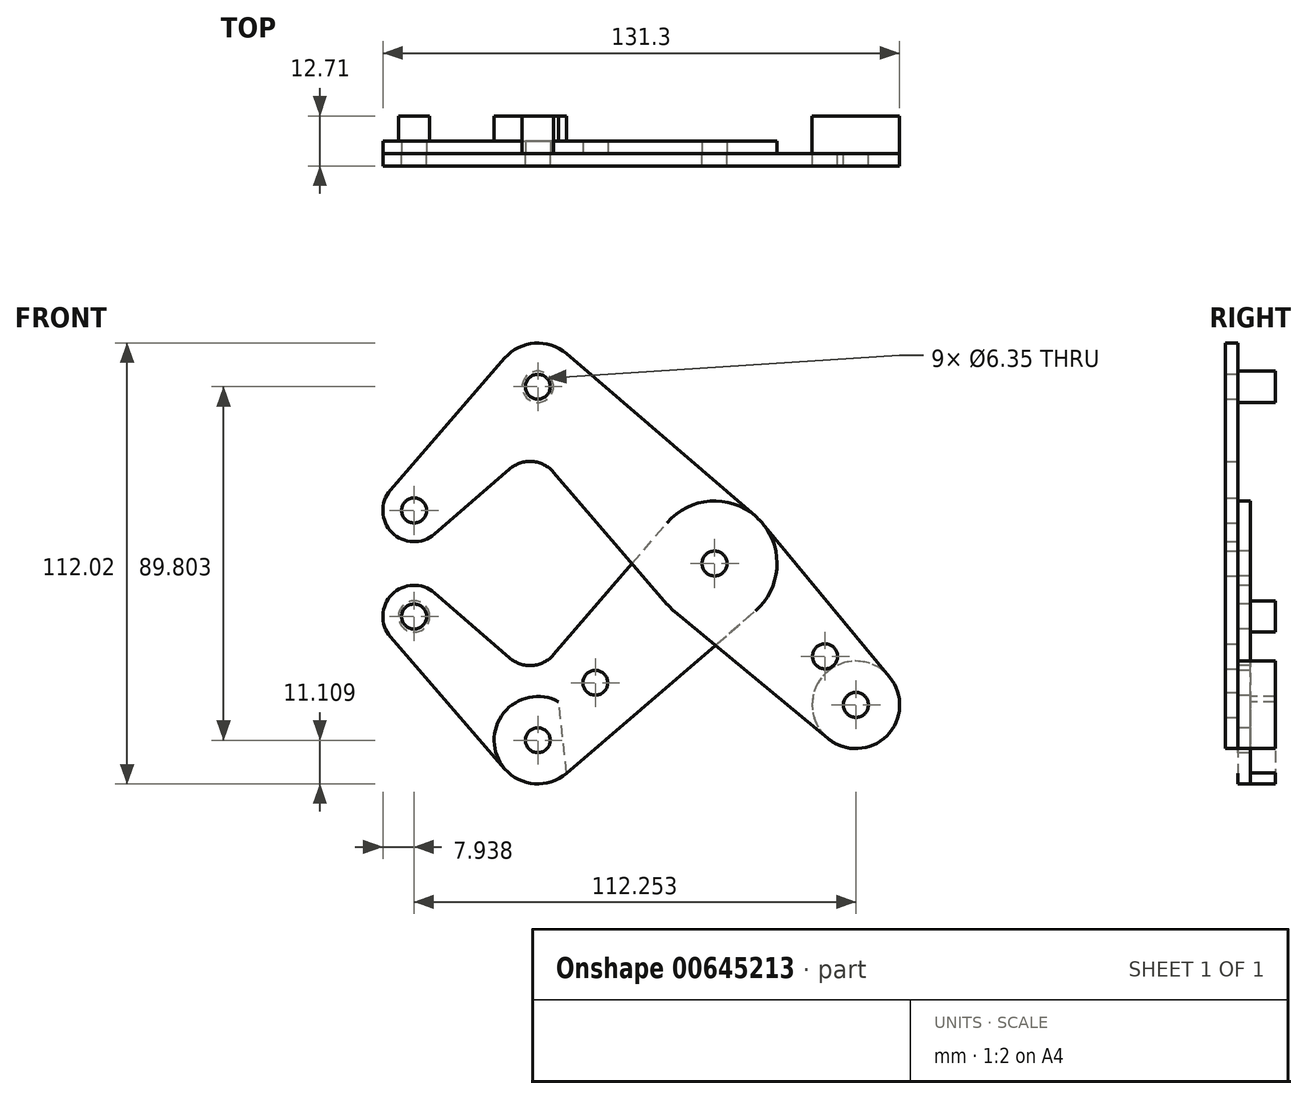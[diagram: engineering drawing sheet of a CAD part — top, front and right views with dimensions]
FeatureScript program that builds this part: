
annotation { "Feature Type Name" : "Feature", "Feature Type Description" : "" }
export const myFeature = defineFeature(function(context is Context, id is Id, definition is map)
    precondition{}
    {
        {
            var Q0;
            Q0=qCreatedBy(makeId("Front.planeOp"),FACE);
            var sketch = newSketch(context, id + "F0", { "sketchPlane" : qUnion([Q0])});
            skLineSegment(sketch, "E0", {"start": v(-76.33, 13.47) * mm, "end": v(-44.9, 44.9) * mm, "construction": true});
            skLineSegment(sketch, "E1", {"start": v(-44.9, 44.9) * mm, "end": v(35.92, -35.92) * mm, "construction": true});
            skCircle(sketch, "E2", {"center": v(-76.33, 13.47) * mm, "radius": 3.18 * mm});
            skCircle(sketch, "E3", {"center": v(-76.33, 13.47) * mm, "radius": 7.94 * mm});
            skCircle(sketch, "E4", {"center": v(-44.9, 44.9) * mm, "radius": 3.18 * mm});
            skCircle(sketch, "E5", {"center": v(-44.9, 44.9) * mm, "radius": 11.11 * mm});
            skCircle(sketch, "E6", {"center": v(0, 0) * mm, "radius": 15.88 * mm});
            skCircle(sketch, "E7", {"center": v(0, 0) * mm, "radius": 3.98 * mm});
            skCircle(sketch, "E8", {"center": v(0, 0) * mm, "radius": 3.18 * mm});
            skCircle(sketch, "E9", {"center": v(35.92, -35.92) * mm, "radius": 11.11 * mm});
            skCircle(sketch, "E10", {"center": v(35.92, -35.92) * mm, "radius": 3.18 * mm});
            skCircle(sketch, "E11", {"center": v(28.07, -23.58) * mm, "radius": 3.18 * mm});
            skLineSegment(sketch, "E12", {"start": v(0, 0) * mm, "end": v(28.01, 28.01) * mm, "construction": true});
            skLineSegment(sketch, "E13", {"start": v(-53.3, 52.18) * mm, "end": v(-82.33, 18.67) * mm});
            skLineSegment(sketch, "E14", {"start": v(-71.13, 7.47) * mm, "end": v(-52.08, 23.98) * mm});
            skLineSegment(sketch, "E15", {"start": v(-40.85, 23.15) * mm, "end": v(-12.04, -10.35) * mm});
            skLineSegment(sketch, "E16", {"start": v(-37.66, 53.33) * mm, "end": v(11.26, 11.26) * mm});
            skLineSegment(sketch, "E17", {"start": v(-10.12, -12.23) * mm, "end": v(28.83, -44.48) * mm});
            skLineSegment(sketch, "E18", {"start": v(12.23, 10.12) * mm, "end": v(44.48, -28.83) * mm});
            skArc(sketch, "E19.filletArc", {"start": v(-40.85, 23.15) * mm, "mid": v(-46.3, 25.9) * mm, "end": v(-52.08, 23.98) * mm});
            skLineSegment(sketch, "E20", {"start": v(0, 0) * mm, "end": v(-44.9, -44.9) * mm, "construction": true});
            skLineSegment(sketch, "E21", {"start": v(-44.9, -44.9) * mm, "end": v(-76.33, -13.47) * mm, "construction": true});
            skCircle(sketch, "E22", {"center": v(-30.3, -30.3) * mm, "radius": 3.18 * mm});
            skCircle(sketch, "E23", {"center": v(-44.9, -44.9) * mm, "radius": 11.11 * mm});
            skCircle(sketch, "E24", {"center": v(-44.9, -44.9) * mm, "radius": 3.18 * mm});
            skCircle(sketch, "E25", {"center": v(-76.33, -13.47) * mm, "radius": 7.94 * mm});
            skCircle(sketch, "E26", {"center": v(-76.33, -13.47) * mm, "radius": 3.18 * mm});
            skLineSegment(sketch, "E27", {"start": v(-82.33, -18.67) * mm, "end": v(-53.3, -52.18) * mm});
            skLineSegment(sketch, "E28", {"start": v(-71.13, -7.47) * mm, "end": v(-52.08, -23.98) * mm});
            skLineSegment(sketch, "E29", {"start": v(-40.85, -23.15) * mm, "end": v(-12.04, 10.35) * mm});
            skLineSegment(sketch, "E30", {"start": v(-37.66, -53.33) * mm, "end": v(10.35, -12.04) * mm});
            skArc(sketch, "E31.filletArc", {"start": v(-52.08, -23.98) * mm, "mid": v(-46.3, -25.9) * mm, "end": v(-40.85, -23.15) * mm});
            skSolve(sketch);
        }
        {
            var Q0;
            Q0=makeQuery(id+"F0.imprint","IMPRINT",FACE,{"disambiguationData":[TD([[makeQuery(id+"F0.imprint","IMPRINT",EDGE,{"derivedFrom":sQuery(id+"F0.wireOp",EDGE,"E2")}),-1.0]])]});
            var Q1;
            {var subQ0=sQuery(id+"F0.wireOp",EDGE,"E13");Q1=makeQuery(id+"F0.imprint","IMPRINT",FACE,{"disambiguationData":[TD([[makeQuery(id+"F0.imprint","IMPRINT",EDGE,{"derivedFrom":subQ0}),1.0]])]});}
            var Q2;
            Q2=makeQuery(id+"F0.imprint","IMPRINT",FACE,{"disambiguationData":[TD([[makeQuery(id+"F0.imprint","IMPRINT",EDGE,{"derivedFrom":sQuery(id+"F0.wireOp",EDGE,"E4")}),-1.0]])]});
            var Q3;
            {var subQ0=sQuery(id+"F0.wireOp",EDGE,"E15");var subQ1=sQuery(id+"F0.wireOp",EDGE,"E6");var subQ2=makeQuery(id+"F0.imprint","INTERSECT",VERTEX,{"derivedFrom":[subQ1,subQ0]});Q3=makeQuery(id+"F0.imprint","IMPRINT",FACE,{"disambiguationData":[TD([[makeQuery(id+"F0.imprint","IMPRINT",EDGE,{"disambiguationData":[TD([[subQ2,1.0]])],"derivedFrom":subQ1}),-1.0]])]});}
            var Q4;
            Q4=makeQuery(id+"F0.imprint","IMPRINT",FACE,{"disambiguationData":[TD([[makeQuery(id+"F0.imprint","IMPRINT",EDGE,{"derivedFrom":sQuery(id+"F0.wireOp",EDGE,"E7")}),-1.0]])]});
            var Q5;
            Q5=makeQuery(id+"F0.imprint","IMPRINT",FACE,{"disambiguationData":[TD([[makeQuery(id+"F0.imprint","IMPRINT",EDGE,{"derivedFrom":sQuery(id+"F0.wireOp",EDGE,"E7")}),1.0]])]});
            var Q6;
            {var subQ0=sQuery(id+"F0.wireOp",EDGE,"E17");var subQ1=sQuery(id+"F0.wireOp",EDGE,"E6");var subQ2=makeQuery(id+"F0.imprint","INTERSECT",VERTEX,{"derivedFrom":[subQ1,subQ0]});Q6=makeQuery(id+"F0.imprint","IMPRINT",FACE,{"disambiguationData":[TD([[makeQuery(id+"F0.imprint","IMPRINT",EDGE,{"disambiguationData":[TD([[subQ2,-1.0]])],"derivedFrom":subQ1}),-1.0]])]});}
            var Q7;
            Q7=makeQuery(id+"F0.imprint","IMPRINT",FACE,{"disambiguationData":[TD([[makeQuery(id+"F0.imprint","IMPRINT",EDGE,{"derivedFrom":sQuery(id+"F0.wireOp",EDGE,"E11")}),-1.0]])]});
            var Q8;
            Q8=makeQuery(id+"F0.imprint","IMPRINT",FACE,{"disambiguationData":[TD([[makeQuery(id+"F0.imprint","IMPRINT",EDGE,{"derivedFrom":sQuery(id+"F0.wireOp",EDGE,"E10")}),-1.0]])]});
            extrude(context, id + "F1", {"entities" : qUnion([Q0, Q1, Q2, Q3, Q4, Q5, Q6, Q7, Q8]), "depth" : 3.17 * mm, "offsetDistance" : 25.4 * mm});
        }
        {
            var Q0;
            Q0=makeQuery(id+"F0.imprint","IMPRINT",FACE,{"disambiguationData":[TD([[makeQuery(id+"F0.imprint","IMPRINT",EDGE,{"derivedFrom":sQuery(id+"F0.wireOp",EDGE,"E26")}),-1.0]])]});
            var Q1;
            Q1=makeQuery(id+"F0.imprint","IMPRINT",FACE,{"disambiguationData":[TD([[makeQuery(id+"F0.imprint","IMPRINT",EDGE,{"derivedFrom":sQuery(id+"F0.wireOp",EDGE,"E24")}),-1.0]])]});
            var Q2;
            Q2=makeQuery(id+"F0.imprint","IMPRINT",FACE,{"disambiguationData":[TD([[makeQuery(id+"F0.imprint","IMPRINT",EDGE,{"derivedFrom":sQuery(id+"F0.wireOp",EDGE,"E22")}),-1.0]])]});
            var Q3;
            {var subQ0=sQuery(id+"F0.wireOp",EDGE,"E17");var subQ1=sQuery(id+"F0.wireOp",EDGE,"E6");var subQ2=makeQuery(id+"F0.imprint","INTERSECT",VERTEX,{"derivedFrom":[subQ1,subQ0]});Q3=makeQuery(id+"F0.imprint","IMPRINT",FACE,{"disambiguationData":[TD([[makeQuery(id+"F0.imprint","IMPRINT",EDGE,{"disambiguationData":[TD([[subQ2,-1.0]])],"derivedFrom":subQ1}),-1.0]])]});}
            var Q4;
            Q4=makeQuery(id+"F0.imprint","IMPRINT",FACE,{"disambiguationData":[TD([[makeQuery(id+"F0.imprint","IMPRINT",EDGE,{"derivedFrom":sQuery(id+"F0.wireOp",EDGE,"E7")}),-1.0]])]});
            var Q5;
            {var subQ0=sQuery(id+"F0.wireOp",EDGE,"E15");var subQ1=sQuery(id+"F0.wireOp",EDGE,"E6");var subQ2=makeQuery(id+"F0.imprint","INTERSECT",VERTEX,{"derivedFrom":[subQ1,subQ0]});Q5=makeQuery(id+"F0.imprint","IMPRINT",FACE,{"disambiguationData":[TD([[makeQuery(id+"F0.imprint","IMPRINT",EDGE,{"disambiguationData":[TD([[subQ2,1.0]])],"derivedFrom":subQ1}),-1.0]])]});}
            var Q6;
            Q6=makeQuery(id+"F0.imprint","IMPRINT",FACE,{"disambiguationData":[TD([[makeQuery(id+"F0.imprint","IMPRINT",EDGE,{"derivedFrom":sQuery(id+"F0.wireOp",EDGE,"E7")}),1.0]])]});
            extrude(context, id + "F2", {"entities" : qUnion([Q0, Q1, Q2, Q3, Q4, Q5, Q6]), "oppositeDirection" : true, "depth" : 3.17 * mm, "offsetDistance" : 25.4 * mm});
        }
        {
            var Q0;
            Q0=makeQuery(id+"F1.opExtrude","CAP_FACE",FACE,{"disambiguationData":[OSD([sQuery(id+"F0.wireOp",EDGE,"E2"),sQuery(id+"F0.wireOp",EDGE,"E3"),sQuery(id+"F0.wireOp",EDGE,"E4"),sQuery(id+"F0.wireOp",EDGE,"E5"),sQuery(id+"F0.wireOp",EDGE,"E6"),sQuery(id+"F0.wireOp",EDGE,"E8"),sQuery(id+"F0.wireOp",EDGE,"E9"),sQuery(id+"F0.wireOp",EDGE,"E10"),sQuery(id+"F0.wireOp",EDGE,"E11"),sQuery(id+"F0.wireOp",EDGE,"E13"),sQuery(id+"F0.wireOp",EDGE,"E14"),sQuery(id+"F0.wireOp",EDGE,"E15"),sQuery(id+"F0.wireOp",EDGE,"E16"),sQuery(id+"F0.wireOp",EDGE,"E17"),sQuery(id+"F0.wireOp",EDGE,"E18"),sQuery(id+"F0.wireOp",EDGE,"E19.filletArc")])],"isStart":false});
            var sketch = newSketch(context, id + "F3", { "sketchPlane" : qUnion([Q0])});
            skCircle(sketch, "E32", {"center": v(-44.9, 44.9) * mm, "radius": 3.98 * mm});
            skCircle(sketch, "E33.0", {"center": v(35.92, -35.92) * mm, "radius": 11.11 * mm});
            skSolve(sketch);
        }
        {
            var Q0;
            Q0=makeQuery(id+"F0.imprint","IMPRINT",FACE,{"disambiguationData":[TD([[makeQuery(id+"F0.imprint","IMPRINT",EDGE,{"derivedFrom":sQuery(id+"F0.wireOp",EDGE,"E22")}),-1.0]])]});
            var sketch = newSketch(context, id + "F4", { "sketchPlane" : qUnion([Q0])});
            skCircle(sketch, "E34", {"center": v(-76.33, -13.47) * mm, "radius": 3.98 * mm});
            skArc(sketch, "E35.0", {"start": v(-39.6, -35.14) * mm, "mid": v(-55.95, -46.13) * mm, "end": v(-37.58, -53.26) * mm});
            skLineSegment(sketch, "E36", {"start": v(-44.9, -44.9) * mm, "end": v(35.92, -35.92) * mm, "construction": true});
            skLineSegment(sketch, "E37", {"start": v(-39.6, -35.14) * mm, "end": v(-37.58, -53.26) * mm});
            skSolve(sketch);
        }
        {
            var Q0;
            Q0=qCreatedBy(makeId("Front.planeOp"),FACE);
            cPlane(context, id + "F5", {"entities" : qUnion([Q0]), "cplaneType" : CPlaneType.OFFSET, "offset" : 9.52 * mm, "oppositeDirection" : true, "width" : 152.4 * mm, "height" : 152.4 * mm});
        }
        {
            var Q0;
            Q0 = qSketchRegion(id + "F3", true);
            var Q1;
            Q1 = qSketchRegion(id + "F4", true);
            var Q2;
            Q2=qCreatedBy(id+"F5.planeOp",FACE);
            extrude(context, id + "F6", {"entities" : qUnion([Q0, Q1]), "endBound" : BoundingType.UP_TO_SURFACE, "oppositeDirection" : true, "depth" : 25.4 * mm, "endBoundEntityFace" : qUnion([Q2]), "offsetDistance" : 25.4 * mm});
        }
        {
            var Q0;
            Q0=makeQuery(id+"F1.opExtrude","SWEPT_BODY",BODY,{"disambiguationData":[OSD([sQuery(id+"F0.wireOp",EDGE,"E2"),sQuery(id+"F0.wireOp",EDGE,"E3"),sQuery(id+"F0.wireOp",EDGE,"E4"),sQuery(id+"F0.wireOp",EDGE,"E5"),sQuery(id+"F0.wireOp",EDGE,"E6"),sQuery(id+"F0.wireOp",EDGE,"E8"),sQuery(id+"F0.wireOp",EDGE,"E9"),sQuery(id+"F0.wireOp",EDGE,"E10"),sQuery(id+"F0.wireOp",EDGE,"E11"),sQuery(id+"F0.wireOp",EDGE,"E13"),sQuery(id+"F0.wireOp",EDGE,"E14"),sQuery(id+"F0.wireOp",EDGE,"E15"),sQuery(id+"F0.wireOp",EDGE,"E16"),sQuery(id+"F0.wireOp",EDGE,"E17"),sQuery(id+"F0.wireOp",EDGE,"E18"),sQuery(id+"F0.wireOp",EDGE,"E19.filletArc")])]});
            var Q1;
            Q1=makeQuery(id+"F2.opExtrude","SWEPT_BODY",BODY,{"disambiguationData":[OSD([sQuery(id+"F0.wireOp",EDGE,"E6"),sQuery(id+"F0.wireOp",EDGE,"E8"),sQuery(id+"F0.wireOp",EDGE,"E22"),sQuery(id+"F0.wireOp",EDGE,"E23"),sQuery(id+"F0.wireOp",EDGE,"E24"),sQuery(id+"F0.wireOp",EDGE,"E25"),sQuery(id+"F0.wireOp",EDGE,"E26"),sQuery(id+"F0.wireOp",EDGE,"E27"),sQuery(id+"F0.wireOp",EDGE,"E28"),sQuery(id+"F0.wireOp",EDGE,"E29"),sQuery(id+"F0.wireOp",EDGE,"E30"),sQuery(id+"F0.wireOp",EDGE,"E31.filletArc")])]});
            var Q2;
            Q2=makeQuery(id+"F6.opExtrude","SWEPT_BODY",BODY,{"disambiguationData":[OSD([sQuery(id+"F4.wireOp",EDGE,"E35.0"),sQuery(id+"F4.wireOp",EDGE,"E37")])]});
            var Q3;
            Q3=makeQuery(id+"F6.opExtrude","SWEPT_BODY",BODY,{"disambiguationData":[OSD([sQuery(id+"F4.wireOp",EDGE,"E34")])]});
            var Q4;
            Q4=makeQuery(id+"F6.opExtrude","SWEPT_BODY",BODY,{"disambiguationData":[OSD([sQuery(id+"F3.wireOp",EDGE,"E32")])]});
            var Q5;
            Q5=makeQuery(id+"F6.opExtrude","SWEPT_BODY",BODY,{"disambiguationData":[OSD([sQuery(id+"F3.wireOp",EDGE,"E33.0")])]});
            booleanBodies(context, id + "F7", {"operationType" : BooleanOperationType.SUBTRACTION, "tools" : qUnion([Q0, Q1]), "targets" : qUnion([Q2, Q3, Q4, Q5]), "keepTools" : true});
        }
    });
